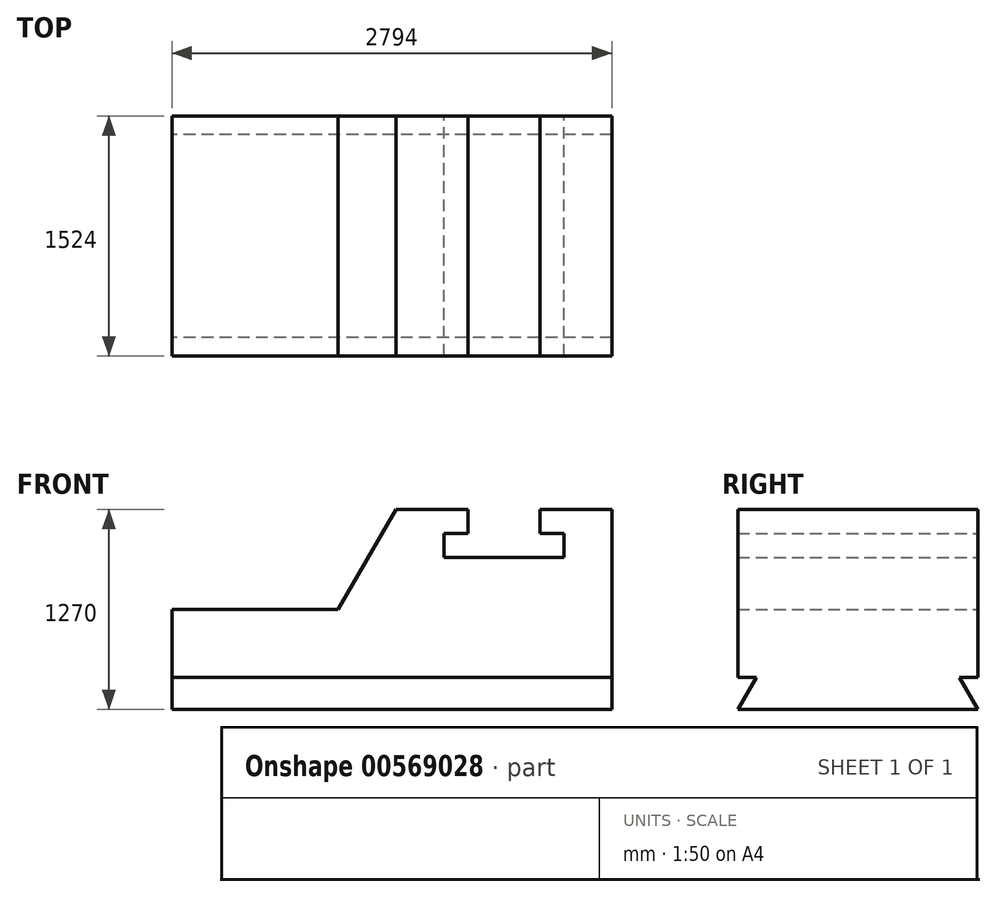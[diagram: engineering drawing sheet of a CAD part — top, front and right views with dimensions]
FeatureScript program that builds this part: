
annotation { "Feature Type Name" : "Feature", "Feature Type Description" : "" }
export const myFeature = defineFeature(function(context is Context, id is Id, definition is map)
    precondition{}
    {
        {
            var Q0;
            Q0=qCreatedBy(makeId("Front.planeOp"),FACE);
            var sketch = newSketch(context, id + "F0", { "sketchPlane" : qUnion([Q0])});
            skLineSegment(sketch, "E0", {"start": v(-351.25, 5.06) * mm, "end": v(2442.75, 5.06) * mm});
            skLineSegment(sketch, "E1", {"start": v(2442.75, 5.06) * mm, "end": v(2442.75, 1071.86) * mm});
            skLineSegment(sketch, "E2", {"start": v(2442.75, 1071.86) * mm, "end": v(1985.55, 1071.86) * mm});
            skLineSegment(sketch, "E3", {"start": v(1985.55, 1071.86) * mm, "end": v(1985.55, 919.46) * mm});
            skLineSegment(sketch, "E4", {"start": v(1985.55, 919.46) * mm, "end": v(2137.95, 919.46) * mm});
            skLineSegment(sketch, "E5", {"start": v(2137.95, 919.46) * mm, "end": v(2137.95, 767.06) * mm});
            skLineSegment(sketch, "E6", {"start": v(2137.95, 767.06) * mm, "end": v(1375.95, 767.06) * mm});
            skLineSegment(sketch, "E7", {"start": v(1375.95, 767.06) * mm, "end": v(1375.95, 919.46) * mm});
            skLineSegment(sketch, "E8", {"start": v(1375.95, 919.46) * mm, "end": v(1528.35, 919.46) * mm});
            skLineSegment(sketch, "E9", {"start": v(1528.35, 919.46) * mm, "end": v(1528.35, 1071.86) * mm});
            skLineSegment(sketch, "E10", {"start": v(1528.35, 1071.86) * mm, "end": v(1071.15, 1071.86) * mm});
            skLineSegment(sketch, "E11", {"start": v(-351.25, 5.06) * mm, "end": v(-351.25, 436.86) * mm});
            skLineSegment(sketch, "E12", {"start": v(-351.25, 436.86) * mm, "end": v(704.53, 436.86) * mm});
            skLineSegment(sketch, "E13", {"start": v(704.53, 436.86) * mm, "end": v(1071.15, 1071.86) * mm});
            skSolve(sketch);
        }
        {
            var Q0;
            Q0=makeQuery(id+"F0.imprint","IMPRINT",FACE,{"disambiguationData":[TD([[makeQuery(id+"F0.imprint","IMPRINT",EDGE,{"derivedFrom":sQuery(id+"F0.wireOp",EDGE,"E0")}),1.0]])]});
            extrude(context, id + "F1", {"entities" : qUnion([Q0]), "depth" : 1524 * mm, "offsetDistance" : 25.4 * mm});
        }
        {
            var Q0;
            Q0=makeQuery(id+"F1.opExtrude","SWEPT_FACE",FACE,{"disambiguationData":[OSD([sQuery(id+"F0.wireOp",EDGE,"E11")])]});
            var sketch = newSketch(context, id + "F2", { "sketchPlane" : qUnion([Q0])});
            skLineSegment(sketch, "E14", {"start": v(0, 5.06) * mm, "end": v(117.32, 5.06) * mm});
            skLineSegment(sketch, "E15", {"start": v(117.32, 5.06) * mm, "end": v(0, -198.14) * mm});
            skLineSegment(sketch, "E16", {"start": v(0, -198.14) * mm, "end": v(1524, -198.14) * mm});
            skLineSegment(sketch, "E17", {"start": v(1524, -198.14) * mm, "end": v(1406.68, 5.06) * mm});
            skLineSegment(sketch, "E18", {"start": v(1406.68, 5.06) * mm, "end": v(1524, 5.06) * mm});
            skSolve(sketch);
        }
        {
            var Q0;
            {var subQ0=sQuery(id+"F2.wireOp",EDGE,"E15");Q0=makeQuery(id+"F2.imprint","IMPRINT",FACE,{"disambiguationData":[TD([[makeQuery(id+"F2.imprint","IMPRINT",EDGE,{"derivedFrom":subQ0}),1.0]])]});}
            extrude(context, id + "F3", {"entities" : qUnion([Q0]), "operationType" : NewBodyOperationType.ADD, "oppositeDirection" : true, "depth" : 2794 * mm, "offsetDistance" : 25.4 * mm});
        }
    });
